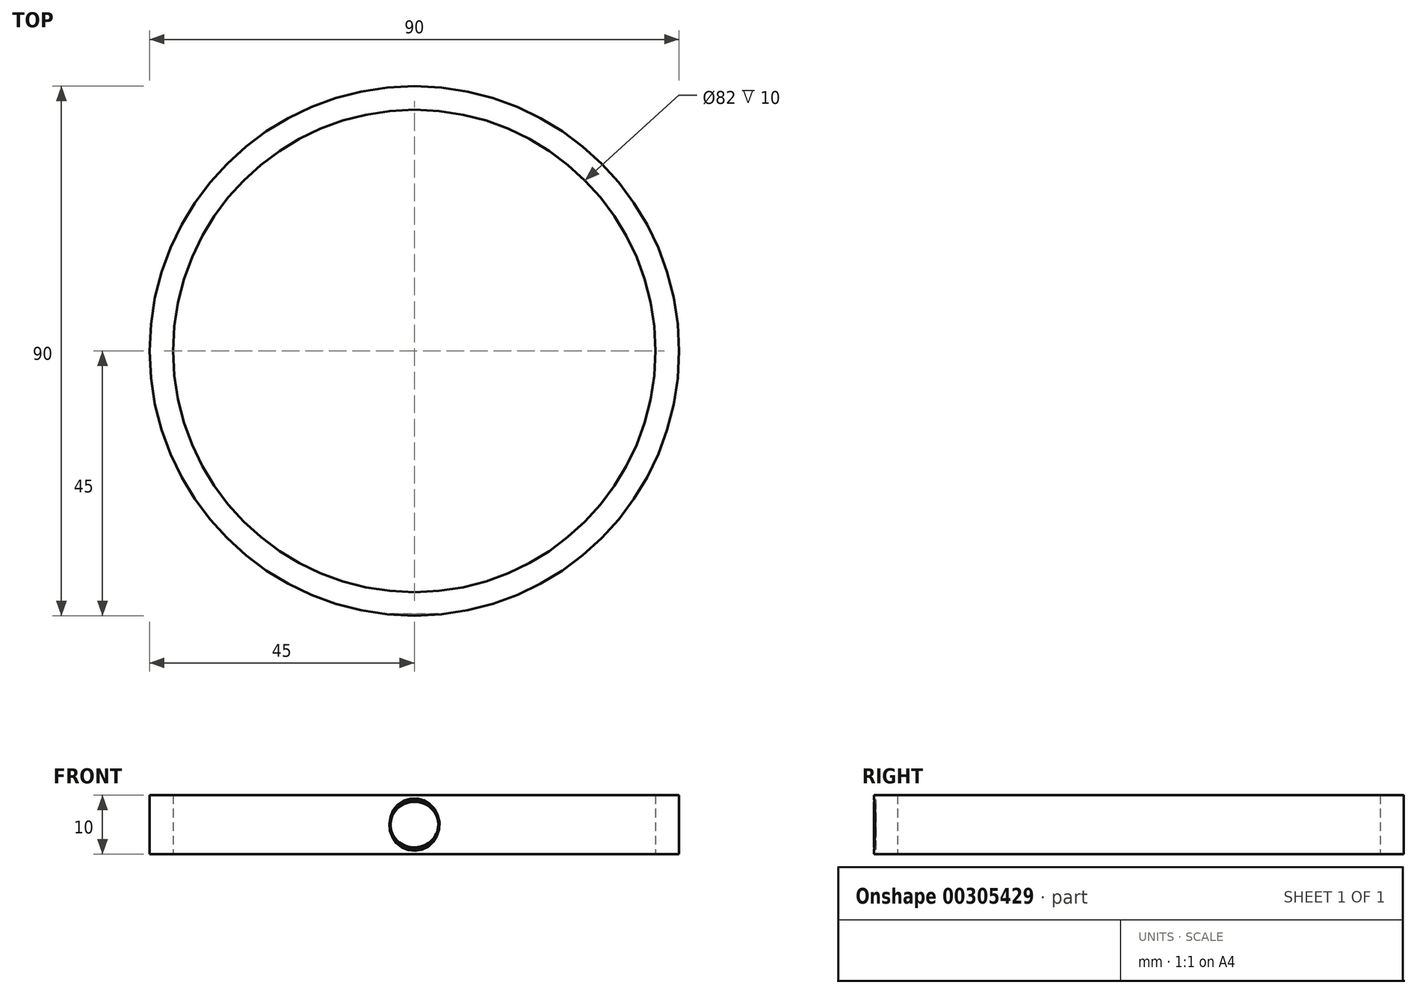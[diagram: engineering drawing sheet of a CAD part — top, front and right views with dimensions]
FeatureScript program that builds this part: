
annotation { "Feature Type Name" : "Feature", "Feature Type Description" : "" }
export const myFeature = defineFeature(function(context is Context, id is Id, definition is map)
    precondition{}
    {
        {
            var Q0;
            Q0=qCreatedBy(makeId("Top.planeOp"),FACE);
            var sketch = newSketch(context, id + "F0", { "sketchPlane" : qUnion([Q0])});
            skCircle(sketch, "E0", {"center": v(0, 0) * mm, "radius": 41 * mm});
            skCircle(sketch, "E1", {"center": v(0, 0) * mm, "radius": 45 * mm});
            skSolve(sketch);
        }
        {
            var Q0;
            Q0=makeQuery(id+"F0.imprint","IMPRINT",FACE,{"disambiguationData":[TD([[makeQuery(id+"F0.imprint","IMPRINT",EDGE,{"derivedFrom":sQuery(id+"F0.wireOp",EDGE,"E0")}),-1.0]])]});
            extrude(context, id + "F1", {"entities" : qUnion([Q0]), "depth" : 10 * mm});
        }
        {
            var Q0;
            Q0=qCreatedBy(makeId("Front.planeOp"),FACE);
            cPlane(context, id + "F2", {"entities" : qUnion([Q0]), "cplaneType" : CPlaneType.OFFSET, "offset" : 45 * mm, "width" : 150 * mm, "height" : 150 * mm});
        }
        {
            var Q0;
            Q0=qCreatedBy(id+"F2.planeOp",FACE);
            var sketch = newSketch(context, id + "F3", { "sketchPlane" : qUnion([Q0])});
            skCircle(sketch, "E2", {"center": v(0, 5) * mm, "radius": 4.47 * mm});
            skLineSegment(sketch, "E3.0", {"start": v(-45, 10) * mm, "end": v(45, 10) * mm, "construction": true});
            skLineSegment(sketch, "E4.0", {"start": v(-45, 0) * mm, "end": v(45, 0) * mm, "construction": true});
            skPoint(sketch, "E5", {"position": v(0, 10) * mm});
            skPoint(sketch, "E6", {"position": v(0, 0) * mm});
            skSolve(sketch);
        }
        {
            var Q0;
            Q0=makeQuery(id+"F1.opExtrude","CAP_FACE",FACE,{"disambiguationData":[OSD([sQuery(id+"F0.wireOp",EDGE,"E0"),sQuery(id+"F0.wireOp",EDGE,"E1")])],"isStart":true});
            var Q1;
            Q1=makeQuery(id+"F1.opExtrude","CAP_FACE",FACE,{"disambiguationData":[OSD([sQuery(id+"F0.wireOp",EDGE,"E0"),sQuery(id+"F0.wireOp",EDGE,"E1")])],"isStart":false});
            cPlane(context, id + "F4", {"entities" : qUnion([Q0, Q1]), "cplaneType" : CPlaneType.MID_PLANE, "offset" : 25 * mm, "width" : 150 * mm, "height" : 150 * mm});
        }
        {
            var Q0;
            Q0=qCreatedBy(id+"F4.planeOp",FACE);
            var sketch = newSketch(context, id + "F5", { "sketchPlane" : qUnion([Q0])});
            skLineSegment(sketch, "E7.0", {"start": v(-4.47, 45) * mm, "end": v(4.47, 45) * mm, "construction": true});
            skLineSegment(sketch, "E8", {"start": v(4.47, 45) * mm, "end": v(4.17, 44.7) * mm});
            skLineSegment(sketch, "E9", {"start": v(4.17, 44.7) * mm, "end": v(3.88, 45) * mm});
            skLineSegment(sketch, "E10", {"start": v(4.47, 45) * mm, "end": v(3.88, 45) * mm});
            skSolve(sketch);
        }
        {
            var Q0;
            Q0 = qSketchRegion(id + "F5", true);
            var Q1;
            Q1=sQuery(id+"F3.wireOp",EDGE,"E2");
            sweep(context, id + "F6", {"operationType" : NewBodyOperationType.REMOVE, "profiles" : qUnion([Q0]), "path" : qUnion([Q1])});
        }
    });
